# Revit family: Toilet-Elongated-Two-Piece-American_Standard-Portsmouth_Champion-213XA_Series
name_source: partatom
category: Plumbing Fixtures
revit_build: Autodesk Revit 2014 (Build: 20130308_1515(x64)
units: mm (PartAtom-declared; Revit-internal decimal feet)

## types (4) — shared parameters
Assembly Code = D2010110
Bowl Shape = Elongated
CW Connection = Yes
CWFU = 5
Cold Water Connection Diameter = 1/2"
Cold Water Connection Height = 4 1/2"
Cold Water Connection Radius = 1/4"
Cold Water Connection Width = 6"
Flush Rate = 1.28 gpf / 4.8 Lpf
HW Connection = No
Installation Type = Floor Mounted
Length = 30 1/4"
Manufacturer = American Standard
Price = Prices may vary. Please consult Manufacturer Representative for most up-to-date price list.
Product Documentation Link = https://www.americanstandard-us.com
Product Page URL = https://www.americanstandard-us.com
Revised Date = 02/22/2017
URL = http://www.americanstandard-us.com
Vent Connection = No
WFU = 5
Warranty Information = 10 Year Warranty
Waste Connection = Yes
Waste Connection Diameter = 2 3/8"
Waste Connection Radius = 1 3/16"
Width = 16 5/8"
zero-valued in all types: HWFU

## per-type parameters (varying)
| type | ADA Compliant | Default Elevation | Description | Finish | Height | Material |
| 213AA.104.020 | Yes | 16 1/2" | Portsmouth Champion Pro Right Height Elongated Toilet | Vitreous China-American Standard-020-White | 31 1/8" | Vitreous China-American Standard-020-White |
| 213CA.104.020 | No | 15" | Portsmouth Champion Pro Elongated Toilet | Vitreous China-American Standard-020-White | 29 5/8" | Vitreous China-American Standard-020-White |
| 213AA.104.222 | Yes | 16 1/2" | Portsmouth Champion Pro Right Height Elongated Toilet | Vitreous China-American Standard-222-Linen | 31 1/8" | Vitreous China-American Standard-222-Linen |
| 213CA.104.222 | No | 15" | Portsmouth Champion Pro Elongated Toilet | Vitreous China-American Standard-222-Linen | 29 5/8" | Vitreous China-American Standard-222-Linen |

note: column(s) folded — value = type name in every type: Model

## geometry (parser evidence)
native form markers: Sweep x3
no freeform markers — native parametric forms only
